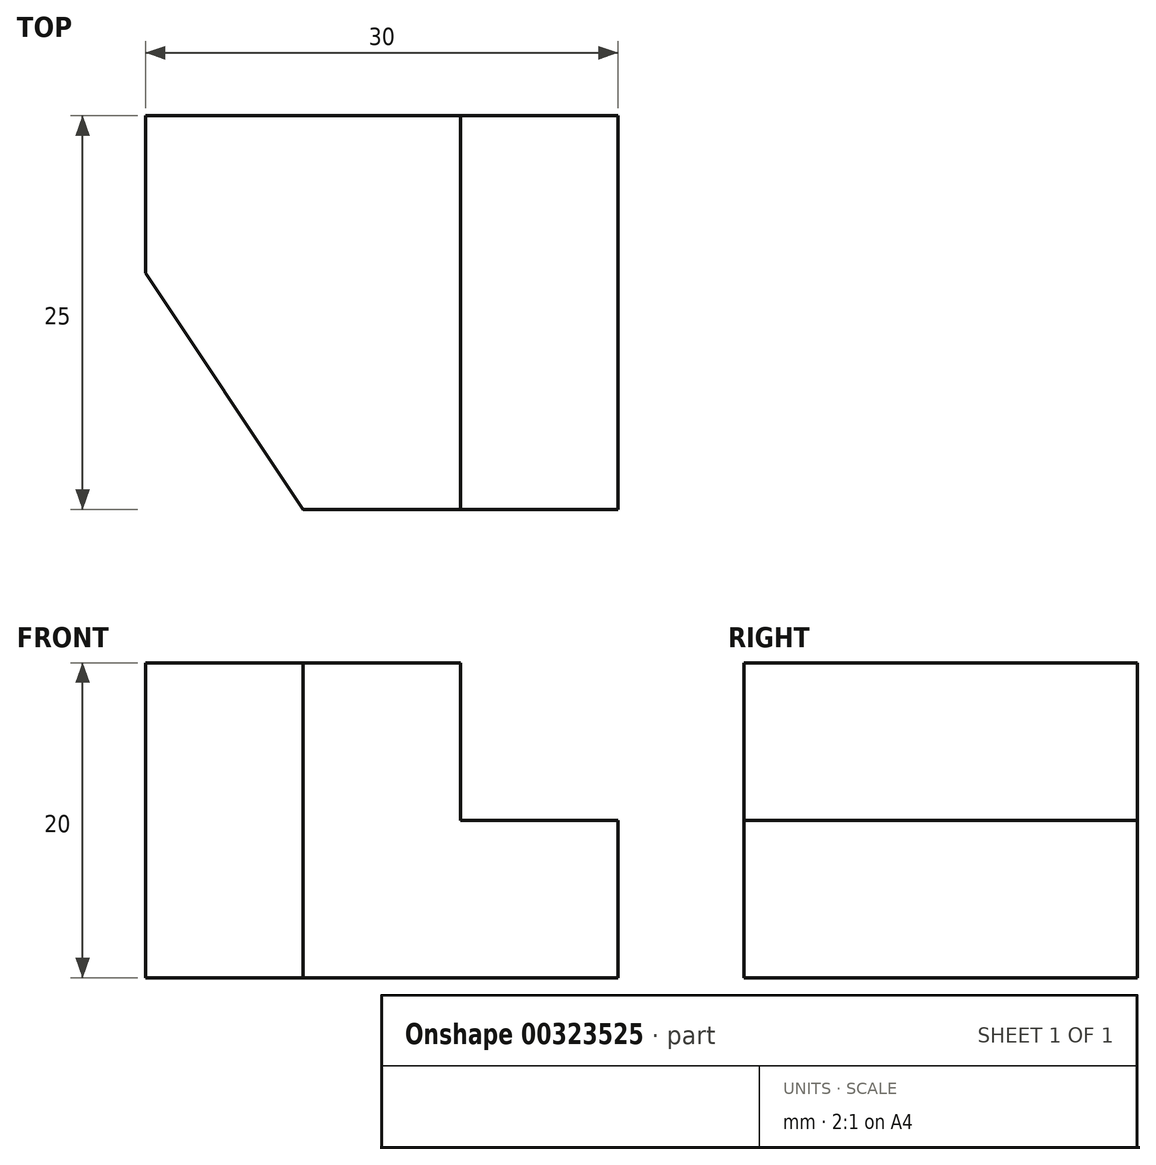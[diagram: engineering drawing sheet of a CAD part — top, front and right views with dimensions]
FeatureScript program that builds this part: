
annotation { "Feature Type Name" : "Feature", "Feature Type Description" : "" }
export const myFeature = defineFeature(function(context is Context, id is Id, definition is map)
    precondition{}
    {
        {
            var Q0;
            Q0=qCreatedBy(makeId("Front.planeOp"),FACE);
            var sketch = newSketch(context, id + "F0", { "sketchPlane" : qUnion([Q0])});
            skLineSegment(sketch, "E0", {"start": v(0, 0) * mm, "end": v(0, 20) * mm});
            skLineSegment(sketch, "E1", {"start": v(0, 20) * mm, "end": v(20, 20) * mm});
            skLineSegment(sketch, "E2", {"start": v(20, 20) * mm, "end": v(20, 10) * mm});
            skLineSegment(sketch, "E3", {"start": v(20, 10) * mm, "end": v(30, 10) * mm});
            skLineSegment(sketch, "E4", {"start": v(30, 10) * mm, "end": v(30, 0) * mm});
            skLineSegment(sketch, "E5", {"start": v(30, 0) * mm, "end": v(0, 0) * mm});
            skLineSegment(sketch, "E6", {"start": v(10, 20) * mm, "end": v(10, 0) * mm});
            skSolve(sketch);
        }
        {
            var Q0;
            Q0 = qSketchRegion(id + "F0", true);
            extrude(context, id + "F1", {"entities" : qUnion([Q0]), "depth" : 25 * mm});
        }
        {
            var Q0;
            Q0=makeQuery(id+"F1.opExtrude","SWEPT_FACE",FACE,{"disambiguationData":[OSD([sQuery(id+"F0.wireOp",EDGE,"E1")])]});
            var sketch = newSketch(context, id + "F2", { "sketchPlane" : qUnion([Q0])});
            skLineSegment(sketch, "E7", {"start": v(0, 0) * mm, "end": v(0, -10) * mm});
            skLineSegment(sketch, "E8", {"start": v(0, -10) * mm, "end": v(10, -25) * mm});
            skLineSegment(sketch, "E9", {"start": v(10, -25) * mm, "end": v(20, -25) * mm});
            skLineSegment(sketch, "E10", {"start": v(20, -25) * mm, "end": v(20, 0) * mm});
            skLineSegment(sketch, "E11", {"start": v(20, 0) * mm, "end": v(0, 0) * mm});
            skSolve(sketch);
        }
        {
            var Q0;
            {var subQ0=sQuery(id+"F2.wireOp",EDGE,"E8");Q0=makeQuery(id+"F2.imprint","IMPRINT",FACE,{"disambiguationData":[TD([[makeQuery(id+"F2.imprint","IMPRINT",EDGE,{"derivedFrom":subQ0}),-1.0]])]});}
            extrude(context, id + "F3", {"entities" : qUnion([Q0]), "operationType" : NewBodyOperationType.REMOVE, "endBound" : BoundingType.THROUGH_ALL, "oppositeDirection" : true, "depth" : 25 * mm});
        }
    });
